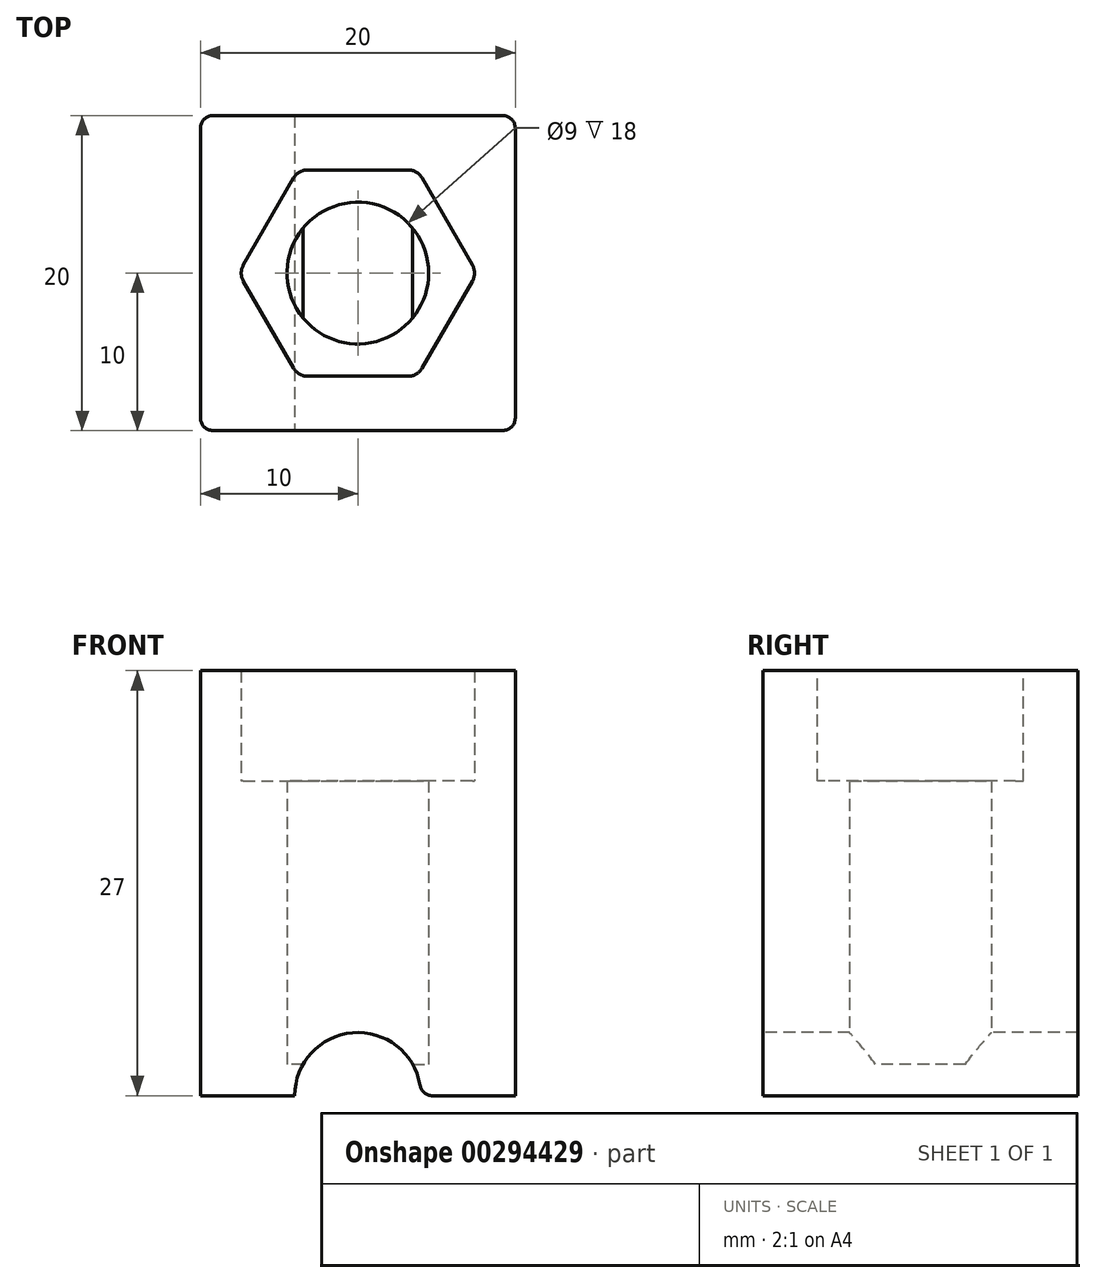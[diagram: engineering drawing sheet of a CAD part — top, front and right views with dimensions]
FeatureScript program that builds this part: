
annotation { "Feature Type Name" : "Feature", "Feature Type Description" : "" }
export const myFeature = defineFeature(function(context is Context, id is Id, definition is map)
    precondition{}
    {
        {
            var Q0;
            Q0=qCreatedBy(makeId("Top.planeOp"),FACE);
            var sketch = newSketch(context, id + "F0", { "sketchPlane" : qUnion([Q0])});
            skLineSegment(sketch, "E0.bottom", {"start": v(-10, -10) * mm, "end": v(10, -10) * mm});
            skLineSegment(sketch, "E0.top", {"start": v(-10, 10) * mm, "end": v(10, 10) * mm});
            skLineSegment(sketch, "E0.left", {"start": v(-10, -10) * mm, "end": v(-10, 10) * mm});
            skLineSegment(sketch, "E0.right", {"start": v(10, -10) * mm, "end": v(10, 10) * mm});
            skPoint(sketch, "E0.middle", {"position": v(0, 0) * mm});
            skSolve(sketch);
        }
        {
            var Q0;
            Q0 = qSketchRegion(id + "F0", true);
            extrude(context, id + "F1", {"entities" : qUnion([Q0]), "depth" : 2 * mm});
        }
        {
            var Q0;
            Q0=makeQuery(id+"F1.opExtrude","CAP_FACE",FACE,{"disambiguationData":[OSD([sQuery(id+"F0.wireOp",EDGE,"E0.bottom"),sQuery(id+"F0.wireOp",EDGE,"E0.top"),sQuery(id+"F0.wireOp",EDGE,"E0.left"),sQuery(id+"F0.wireOp",EDGE,"E0.right")])],"isStart":false});
            var sketch = newSketch(context, id + "F2", { "sketchPlane" : qUnion([Q0])});
            skLineSegment(sketch, "E1.bottom", {"start": v(-4.5, -4.5) * mm, "end": v(4.5, -4.5) * mm});
            skLineSegment(sketch, "E1.top", {"start": v(-4.5, 4.5) * mm, "end": v(4.5, 4.5) * mm});
            skLineSegment(sketch, "E1.left", {"start": v(-4.5, -4.5) * mm, "end": v(-4.5, 4.5) * mm});
            skLineSegment(sketch, "E1.right", {"start": v(4.5, -4.5) * mm, "end": v(4.5, 4.5) * mm});
            skPoint(sketch, "E1.middle", {"position": v(0, 0) * mm});
            skCircle(sketch, "E2", {"center": v(0, 0) * mm, "radius": 4.5 * mm});
            skSolve(sketch);
        }
        {
            var Q0;
            Q0=makeQuery(id+"F2.imprint","IMPRINT",FACE,{"disambiguationData":[TD([[makeQuery(id+"F2.imprint","IMPRINT",EDGE,{"derivedFrom":sQuery(id+"F2.wireOp",EDGE,"E1.bottom")}),-1.0]])]});
            extrude(context, id + "F3", {"entities" : qUnion([Q0]), "operationType" : NewBodyOperationType.ADD, "depth" : 25 * mm});
        }
        {
            var Q0;
            {var subQ0=sQuery(id+"F0.wireOp",EDGE,"E0.bottom");Q0=makeQuery(id+"F3.boolean.opBoolean","MERGE",FACE,{"derivedFrom":[makeQuery(id+"F1.opExtrude","SWEPT_FACE",FACE,{"disambiguationData":[OSD([subQ0])]}),makeQuery(id+"F3.opExtrude","SWEPT_FACE",FACE,{"disambiguationData":[OSD([subQ0])]})]});}
            var sketch = newSketch(context, id + "F4", { "sketchPlane" : qUnion([Q0])});
            skCircle(sketch, "E3", {"center": v(0, 0) * mm, "radius": 4 * mm});
            skSolve(sketch);
        }
        {
            var Q0;
            Q0=makeQuery(id+"F3.opExtrude","CAP_FACE",FACE,{"disambiguationData":[OSD([sQuery(id+"F0.wireOp",EDGE,"E0.bottom"),sQuery(id+"F0.wireOp",EDGE,"E0.top"),sQuery(id+"F0.wireOp",EDGE,"E0.left"),sQuery(id+"F0.wireOp",EDGE,"E0.right"),sQuery(id+"F2.wireOp",EDGE,"E1.bottom"),sQuery(id+"F2.wireOp",EDGE,"E1.top"),sQuery(id+"F2.wireOp",EDGE,"E1.left"),sQuery(id+"F2.wireOp",EDGE,"E1.right")])],"isStart":false});
            var sketch = newSketch(context, id + "F5", { "sketchPlane" : qUnion([Q0])});
            skCircle(sketch, "E4.cCircle", {"center": v(0, 0) * mm, "radius": 7.56 * mm, "construction": true});
            skLineSegment(sketch, "E4.0", {"start": v(7.56, 0) * mm, "end": v(3.78, -6.55) * mm});
            skLineSegment(sketch, "E4.1", {"start": v(3.78, -6.55) * mm, "end": v(-3.78, -6.55) * mm});
            skLineSegment(sketch, "E4.2", {"start": v(-3.78, -6.55) * mm, "end": v(-7.56, 0) * mm});
            skLineSegment(sketch, "E4.3", {"start": v(-7.56, 0) * mm, "end": v(-3.78, 6.55) * mm});
            skLineSegment(sketch, "E4.4", {"start": v(-3.78, 6.55) * mm, "end": v(3.78, 6.55) * mm});
            skLineSegment(sketch, "E4.5", {"start": v(3.78, 6.55) * mm, "end": v(7.56, 0) * mm});
            skSolve(sketch);
        }
        {
            var Q0;
            Q0=makeQuery(id+"F5.imprint","IMPRINT",FACE,{"disambiguationData":[TD([[makeQuery(id+"F5.imprint","IMPRINT",EDGE,{"derivedFrom":sQuery(id+"F5.wireOp",EDGE,"E4.0")}),-1.0]])]});
            extrude(context, id + "F6", {"entities" : qUnion([Q0]), "operationType" : NewBodyOperationType.REMOVE, "oppositeDirection" : true, "depth" : 7 * mm});
        }
        {
            var Q0;
            Q0=makeQuery(id+"F6.boolean.opBoolean","COPY",EDGE,{"derivedFrom":makeQuery(id+"F6.opExtrude","SWEPT_EDGE",EDGE,{"disambiguationData":[OSD([sQuery(id+"F5.wireOp",EDGE,"E4.0"),sQuery(id+"F5.wireOp",EDGE,"E4.1")])]})});
            var Q1;
            Q1=makeQuery(id+"F6.boolean.opBoolean","COPY",EDGE,{"derivedFrom":makeQuery(id+"F6.opExtrude","SWEPT_EDGE",EDGE,{"disambiguationData":[OSD([sQuery(id+"F5.wireOp",EDGE,"E4.0"),sQuery(id+"F5.wireOp",EDGE,"E4.5")])]})});
            var Q2;
            Q2=makeQuery(id+"F6.boolean.opBoolean","COPY",EDGE,{"derivedFrom":makeQuery(id+"F6.opExtrude","SWEPT_EDGE",EDGE,{"disambiguationData":[OSD([sQuery(id+"F5.wireOp",EDGE,"E4.4"),sQuery(id+"F5.wireOp",EDGE,"E4.5")])]})});
            var Q3;
            Q3=makeQuery(id+"F6.boolean.opBoolean","COPY",EDGE,{"derivedFrom":makeQuery(id+"F6.opExtrude","SWEPT_EDGE",EDGE,{"disambiguationData":[OSD([sQuery(id+"F5.wireOp",EDGE,"E4.3"),sQuery(id+"F5.wireOp",EDGE,"E4.4")])]})});
            var Q4;
            Q4=makeQuery(id+"F6.boolean.opBoolean","COPY",EDGE,{"derivedFrom":makeQuery(id+"F6.opExtrude","SWEPT_EDGE",EDGE,{"disambiguationData":[OSD([sQuery(id+"F5.wireOp",EDGE,"E4.2"),sQuery(id+"F5.wireOp",EDGE,"E4.3")])]})});
            var Q5;
            Q5=makeQuery(id+"F6.boolean.opBoolean","COPY",EDGE,{"derivedFrom":makeQuery(id+"F6.opExtrude","SWEPT_EDGE",EDGE,{"disambiguationData":[OSD([sQuery(id+"F5.wireOp",EDGE,"E4.1"),sQuery(id+"F5.wireOp",EDGE,"E4.2")])]})});
            fillet(context, id + "F7", {"entities" : qUnion([Q0, Q1, Q2, Q3, Q4, Q5]), "radius" : 1 * mm, "tangentPropagation" : true, "allowEdgeOverflow" : false});
        }
        {
            var Q0;
            Q0=makeQuery(id+"F2.imprint","IMPRINT",FACE,{"disambiguationData":[TD([[makeQuery(id+"F2.imprint","IMPRINT",EDGE,{"derivedFrom":makeQuery(id+"F1.opExtrude","CAP_EDGE",EDGE,{"disambiguationData":[OSD([sQuery(id+"F0.wireOp",EDGE,"E0.bottom")])],"isStart":false})}),1.0]])]});
            var Q1;
            {var subQ0=sQuery(id+"F2.wireOp",EDGE,"E1.right");var subQ1=sQuery(id+"F2.wireOp",EDGE,"E1.bottom");var subQ2=makeQuery(id+"F2.imprint","INTERSECT",VERTEX,{"derivedFrom":[subQ1,subQ0]});Q1=makeQuery(id+"F2.imprint","IMPRINT",FACE,{"disambiguationData":[TD([[makeQuery(id+"F2.imprint","IMPRINT",EDGE,{"disambiguationData":[TD([[subQ2,1.0]])],"derivedFrom":subQ1}),1.0]])]});}
            var Q2;
            {var subQ0=sQuery(id+"F2.wireOp",EDGE,"E1.left");var subQ1=sQuery(id+"F2.wireOp",EDGE,"E1.bottom");var subQ2=makeQuery(id+"F2.imprint","INTERSECT",VERTEX,{"derivedFrom":[subQ1,subQ0]});Q2=makeQuery(id+"F2.imprint","IMPRINT",FACE,{"disambiguationData":[TD([[makeQuery(id+"F2.imprint","IMPRINT",EDGE,{"disambiguationData":[TD([[subQ2,-1.0]])],"derivedFrom":subQ1}),1.0]])]});}
            var Q3;
            {var subQ0=sQuery(id+"F2.wireOp",EDGE,"E1.left");var subQ1=sQuery(id+"F2.wireOp",EDGE,"E1.top");var subQ2=makeQuery(id+"F2.imprint","INTERSECT",VERTEX,{"derivedFrom":[subQ1,subQ0]});Q3=makeQuery(id+"F2.imprint","IMPRINT",FACE,{"disambiguationData":[TD([[makeQuery(id+"F2.imprint","IMPRINT",EDGE,{"disambiguationData":[TD([[subQ2,-1.0]])],"derivedFrom":subQ1}),-1.0]])]});}
            var Q4;
            {var subQ0=sQuery(id+"F2.wireOp",EDGE,"E1.right");var subQ1=sQuery(id+"F2.wireOp",EDGE,"E1.top");var subQ2=makeQuery(id+"F2.imprint","INTERSECT",VERTEX,{"derivedFrom":[subQ1,subQ0]});Q4=makeQuery(id+"F2.imprint","IMPRINT",FACE,{"disambiguationData":[TD([[makeQuery(id+"F2.imprint","IMPRINT",EDGE,{"disambiguationData":[TD([[subQ2,1.0]])],"derivedFrom":subQ1}),-1.0]])]});}
            extrude(context, id + "F8", {"entities" : qUnion([Q0, Q1, Q2, Q3, Q4]), "operationType" : NewBodyOperationType.ADD, "depth" : 18 * mm});
        }
        {
            var Q0;
            {var subQ0=sQuery(id+"F4.wireOp",EDGE,"E3");var subQ1=makeQuery(id+"F1.opExtrude","CAP_EDGE",EDGE,{"disambiguationData":[OSD([sQuery(id+"F0.wireOp",EDGE,"E0.bottom")])],"isStart":true});var subQ2=makeQuery(id+"F4.imprint","INTERSECT",VERTEX,{"disambiguationData":[OD(0.0)],"derivedFrom":[subQ1,subQ0]});Q0=makeQuery(id+"F4.imprint","IMPRINT",FACE,{"disambiguationData":[TD([[makeQuery(id+"F4.imprint","IMPRINT",EDGE,{"disambiguationData":[TD([[subQ2,1.0]])],"derivedFrom":subQ0}),1.0]])]});}
            extrude(context, id + "F9", {"entities" : qUnion([Q0]), "operationType" : NewBodyOperationType.REMOVE, "endBound" : BoundingType.SYMMETRIC, "oppositeDirection" : true, "depth" : 49.6 * mm});
        }
        {
            var Q0;
            {var subQ0=sQuery(id+"F4.wireOp",EDGE,"E3");var subQ1=sQuery(id+"F0.wireOp",EDGE,"E0.bottom");Q0=makeQuery(id+"F9.boolean.opBoolean","COPY",EDGE,{"derivedFrom":makeQuery(id+"F9.opExtrude","SWEPT_EDGE",EDGE,{"disambiguationData":[OSD([subQ1,subQ0]),TDD([makeQuery(id+"F4.imprint","INTERSECT",VERTEX,{"disambiguationData":[OD(1.0)],"derivedFrom":[makeQuery(id+"F1.opExtrude","CAP_EDGE",EDGE,{"disambiguationData":[OSD([subQ1])],"isStart":true}),subQ0]})])]})});}
            var Q1;
            {var subQ0=sQuery(id+"F4.wireOp",EDGE,"E3");var subQ1=sQuery(id+"F0.wireOp",EDGE,"E0.bottom");Q1=makeQuery(id+"F9.boolean.opBoolean","COPY",EDGE,{"derivedFrom":makeQuery(id+"F9.opExtrude","SWEPT_EDGE",EDGE,{"disambiguationData":[OSD([subQ1,subQ0]),TDD([makeQuery(id+"F4.imprint","INTERSECT",VERTEX,{"disambiguationData":[OD(0.0)],"derivedFrom":[makeQuery(id+"F1.opExtrude","CAP_EDGE",EDGE,{"disambiguationData":[OSD([subQ1])],"isStart":true}),subQ0]})])]})});}
            fillet(context, id + "F10", {"entities" : qUnion([Q0, Q1]), "radius" : 0.8 * mm, "tangentPropagation" : true, "allowEdgeOverflow" : false});
        }
        {
            var Q0;
            {var subQ0=sQuery(id+"F0.wireOp",EDGE,"E0.right");var subQ1=sQuery(id+"F0.wireOp",EDGE,"E0.bottom");Q0=makeQuery(id+"F3.boolean.opBoolean","MERGE",EDGE,{"derivedFrom":[makeQuery(id+"F1.opExtrude","SWEPT_EDGE",EDGE,{"disambiguationData":[OSD([subQ1,subQ0])]}),makeQuery(id+"F3.opExtrude","SWEPT_EDGE",EDGE,{"disambiguationData":[OSD([subQ1,subQ0])]})]});}
            var Q1;
            {var subQ0=sQuery(id+"F0.wireOp",EDGE,"E0.left");var subQ1=sQuery(id+"F0.wireOp",EDGE,"E0.bottom");Q1=makeQuery(id+"F3.boolean.opBoolean","MERGE",EDGE,{"derivedFrom":[makeQuery(id+"F1.opExtrude","SWEPT_EDGE",EDGE,{"disambiguationData":[OSD([subQ1,subQ0])]}),makeQuery(id+"F3.opExtrude","SWEPT_EDGE",EDGE,{"disambiguationData":[OSD([subQ1,subQ0])]})]});}
            var Q2;
            {var subQ0=sQuery(id+"F0.wireOp",EDGE,"E0.left");var subQ1=sQuery(id+"F0.wireOp",EDGE,"E0.top");Q2=makeQuery(id+"F3.boolean.opBoolean","MERGE",EDGE,{"derivedFrom":[makeQuery(id+"F1.opExtrude","SWEPT_EDGE",EDGE,{"disambiguationData":[OSD([subQ1,subQ0])]}),makeQuery(id+"F3.opExtrude","SWEPT_EDGE",EDGE,{"disambiguationData":[OSD([subQ1,subQ0])]})]});}
            var Q3;
            {var subQ0=sQuery(id+"F0.wireOp",EDGE,"E0.right");var subQ1=sQuery(id+"F0.wireOp",EDGE,"E0.top");Q3=makeQuery(id+"F3.boolean.opBoolean","MERGE",EDGE,{"derivedFrom":[makeQuery(id+"F1.opExtrude","SWEPT_EDGE",EDGE,{"disambiguationData":[OSD([subQ1,subQ0])]}),makeQuery(id+"F3.opExtrude","SWEPT_EDGE",EDGE,{"disambiguationData":[OSD([subQ1,subQ0])]})]});}
            fillet(context, id + "F11", {"entities" : qUnion([Q0, Q1, Q2, Q3]), "radius" : 0.8 * mm, "tangentPropagation" : true, "allowEdgeOverflow" : false});
        }
    });
